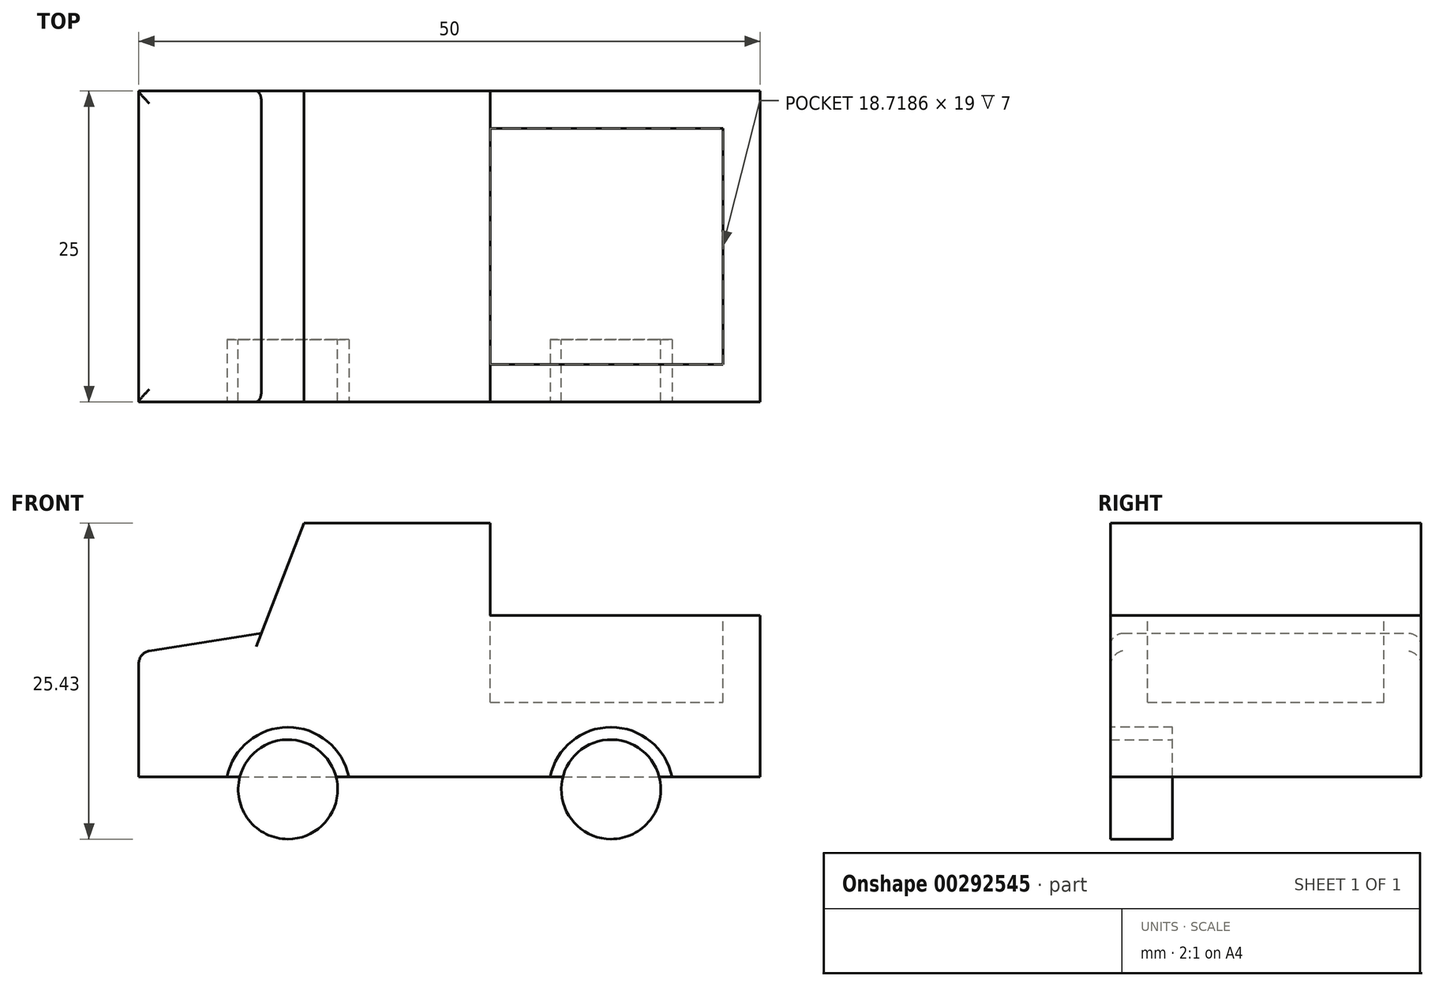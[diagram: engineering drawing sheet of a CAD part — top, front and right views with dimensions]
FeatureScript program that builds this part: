
annotation { "Feature Type Name" : "Feature", "Feature Type Description" : "" }
export const myFeature = defineFeature(function(context is Context, id is Id, definition is map)
    precondition{}
    {
        {
            var Q0;
            Q0=qCreatedBy(makeId("Front.planeOp"),FACE);
            var sketch = newSketch(context, id + "F0", { "sketchPlane" : qUnion([Q0])});
            skLineSegment(sketch, "E0.top", {"start": v(-25, -15) * mm, "end": v(25, -15) * mm});
            skLineSegment(sketch, "E0.left", {"start": v(-25, -5) * mm, "end": v(-25, -15) * mm});
            skLineSegment(sketch, "E0.right", {"start": v(25, -6) * mm, "end": v(25, -15) * mm});
            skLineSegment(sketch, "E1", {"start": v(-25, -5) * mm, "end": v(-15.12, -3.44) * mm});
            skLineSegment(sketch, "E2", {"start": v(-15.12, -3.44) * mm, "end": v(-11.72, 5.43) * mm});
            skLineSegment(sketch, "E3", {"start": v(-11.72, 5.43) * mm, "end": v(3.28, 5.43) * mm});
            skLineSegment(sketch, "E4", {"start": v(3.28, 5.43) * mm, "end": v(3.28, -2) * mm});
            skLineSegment(sketch, "E5", {"start": v(3.28, -2) * mm, "end": v(25, -2) * mm});
            skLineSegment(sketch, "E6", {"start": v(25, -2) * mm, "end": v(25, -6) * mm});
            skSolve(sketch);
        }
        {
            var Q0;
            Q0 = qSketchRegion(id + "F0", true);
            extrude(context, id + "F1", {"entities" : qUnion([Q0]), "depth" : 25 * mm});
        }
        {
            var Q0;
            Q0=makeQuery(id+"F1.opExtrude","SWEPT_FACE",FACE,{"disambiguationData":[OSD([sQuery(id+"F0.wireOp",EDGE,"E5")])]});
            var sketch = newSketch(context, id + "F2", { "sketchPlane" : qUnion([Q0])});
            skLineSegment(sketch, "E7.0", {"start": v(3.28, -25) * mm, "end": v(3.28, 0) * mm});
            skLineSegment(sketch, "E8.bottom", {"start": v(3.28, -3) * mm, "end": v(22, -3) * mm});
            skLineSegment(sketch, "E8.top", {"start": v(3.28, -22) * mm, "end": v(22, -22) * mm});
            skLineSegment(sketch, "E8.left", {"start": v(3.28, -3) * mm, "end": v(3.28, -22) * mm});
            skLineSegment(sketch, "E8.right", {"start": v(22, -3) * mm, "end": v(22, -22) * mm});
            skSolve(sketch);
        }
        {
            var Q0;
            Q0=makeQuery(id+"F2.imprint","IMPRINT",FACE,{"disambiguationData":[TD([[makeQuery(id+"F2.imprint","IMPRINT",EDGE,{"derivedFrom":sQuery(id+"F2.wireOp",EDGE,"E8.bottom")}),-1.0]])]});
            var Q1;
            Q1=makeQuery(id+"F1.opExtrude","SWEPT_FACE",FACE,{"disambiguationData":[OSD([sQuery(id+"F0.wireOp",EDGE,"E0.top")])]});
            extrude(context, id + "F3", {"entities" : qUnion([Q0]), "operationType" : NewBodyOperationType.REMOVE, "oppositeDirection" : true, "endBoundEntityFace" : qUnion([Q1]), "depth" : 7 * mm});
        }
        {
            var Q0;
            Q0=makeQuery(id+"F1.opExtrude","CAP_EDGE",EDGE,{"disambiguationData":[OSD([sQuery(id+"F0.wireOp",EDGE,"E1")])],"isStart":true});
            var Q1;
            Q1=makeQuery(id+"F1.opExtrude","CAP_EDGE",EDGE,{"disambiguationData":[OSD([sQuery(id+"F0.wireOp",EDGE,"E1")])],"isStart":false});
            var Q2;
            Q2=makeQuery(id+"F1.opExtrude","SWEPT_EDGE",EDGE,{"disambiguationData":[OSD([sQuery(id+"F0.wireOp",EDGE,"E0.left"),sQuery(id+"F0.wireOp",EDGE,"E1")])]});
            fillet(context, id + "F4", {"entities" : qUnion([Q0, Q1, Q2]), "radius" : 1 * mm, "tangentPropagation" : true, "allowEdgeOverflow" : false});
        }
        {
            var Q0;
            Q0=makeQuery(id+"F1.opExtrude","CAP_FACE",FACE,{"disambiguationData":[OSD([sQuery(id+"F0.wireOp",EDGE,"E0.top"),sQuery(id+"F0.wireOp",EDGE,"E0.left"),sQuery(id+"F0.wireOp",EDGE,"E0.right"),sQuery(id+"F0.wireOp",EDGE,"E1"),sQuery(id+"F0.wireOp",EDGE,"E2"),sQuery(id+"F0.wireOp",EDGE,"E3"),sQuery(id+"F0.wireOp",EDGE,"E4"),sQuery(id+"F0.wireOp",EDGE,"E5"),sQuery(id+"F0.wireOp",EDGE,"E6")])],"isStart":false});
            var sketch = newSketch(context, id + "F5", { "sketchPlane" : qUnion([Q0])});
            skCircle(sketch, "E9", {"center": v(-13, -16) * mm, "radius": 5 * mm});
            skCircle(sketch, "E10", {"center": v(13, -16) * mm, "radius": 5 * mm});
            skSolve(sketch);
        }
        {
            var Q0;
            Q0 = qSketchRegion(id + "F5", true);
            extrude(context, id + "F6", {"entities" : qUnion([Q0]), "operationType" : NewBodyOperationType.REMOVE, "oppositeDirection" : true, "depth" : 5 * mm, "offsetDistance" : 25 * mm});
        }
        {
            var Q0;
            Q0=makeQuery(id+"F6.boolean.opBoolean","COPY",FACE,{"derivedFrom":makeQuery(id+"F6.opExtrude","CAP_FACE",FACE,{"disambiguationData":[OSD([sQuery(id+"F5.wireOp",EDGE,"E9")])],"isStart":false})});
            var sketch = newSketch(context, id + "F7", { "sketchPlane" : qUnion([Q0])});
            skCircle(sketch, "E11", {"center": v(-13, -16) * mm, "radius": 4 * mm});
            skCircle(sketch, "E12", {"center": v(13, -16) * mm, "radius": 4 * mm});
            skSolve(sketch);
        }
        {
            var Q0;
            Q0 = qSketchRegion(id + "F7", true);
            var Q1;
            Q1=makeQuery(id+"F1.opExtrude","CAP_FACE",FACE,{"disambiguationData":[OSD([sQuery(id+"F0.wireOp",EDGE,"E0.top"),sQuery(id+"F0.wireOp",EDGE,"E0.left"),sQuery(id+"F0.wireOp",EDGE,"E0.right"),sQuery(id+"F0.wireOp",EDGE,"E1"),sQuery(id+"F0.wireOp",EDGE,"E2"),sQuery(id+"F0.wireOp",EDGE,"E3"),sQuery(id+"F0.wireOp",EDGE,"E4"),sQuery(id+"F0.wireOp",EDGE,"E5"),sQuery(id+"F0.wireOp",EDGE,"E6")])],"isStart":false});
            extrude(context, id + "F8", {"entities" : qUnion([Q0]), "operationType" : NewBodyOperationType.ADD, "endBound" : BoundingType.UP_TO_SURFACE, "depth" : 25 * mm, "endBoundEntityFace" : qUnion([Q1]), "offsetDistance" : 25 * mm});
        }
    });
